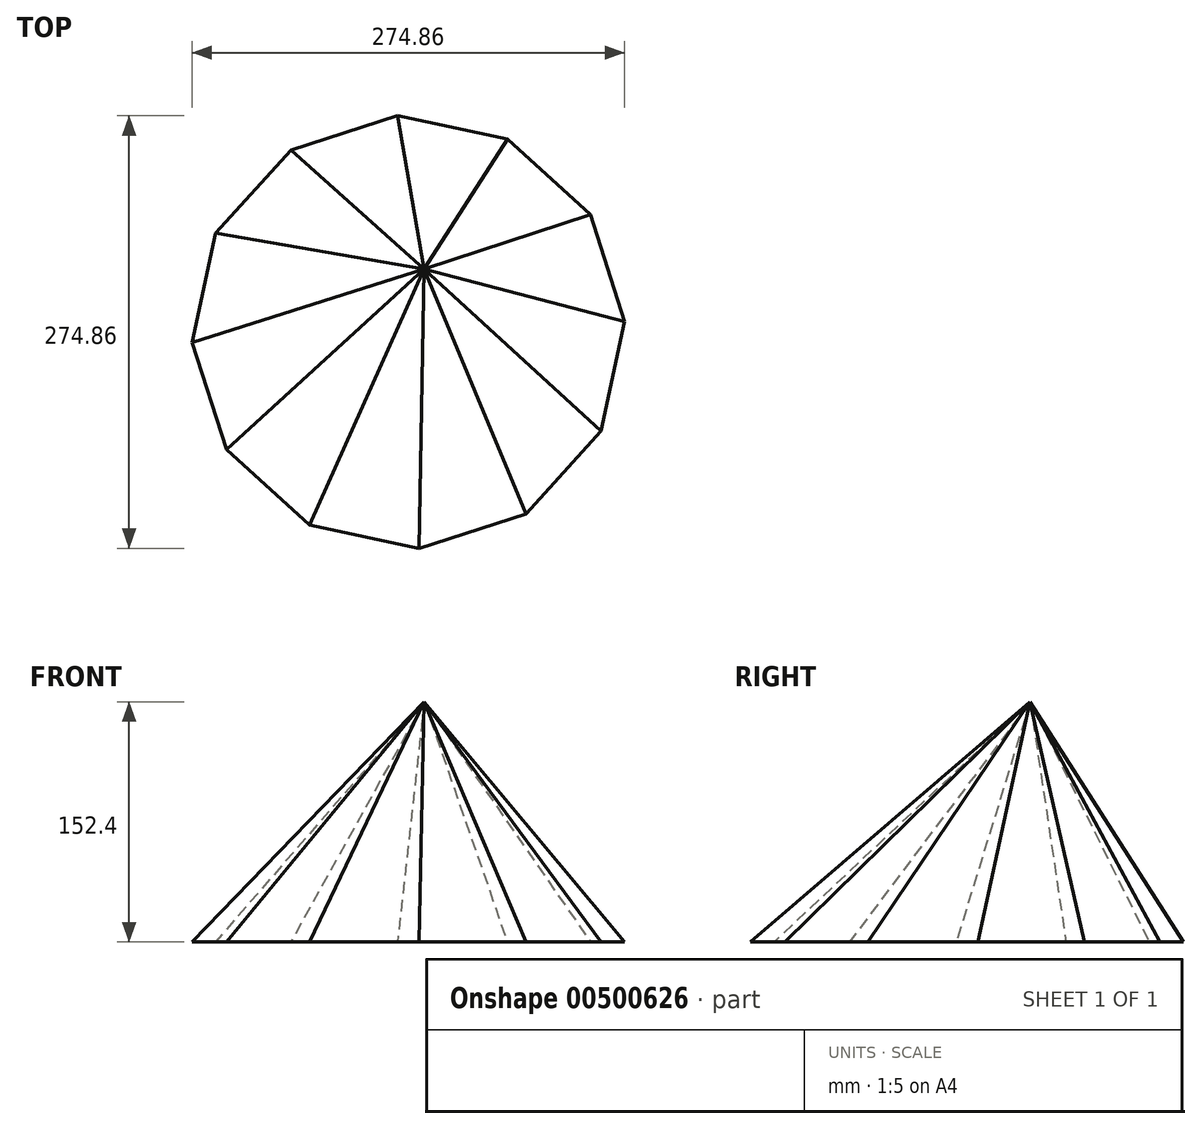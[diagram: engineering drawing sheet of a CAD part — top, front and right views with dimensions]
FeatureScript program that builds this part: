
annotation { "Feature Type Name" : "Feature", "Feature Type Description" : "" }
export const myFeature = defineFeature(function(context is Context, id is Id, definition is map)
    precondition{}
    {
        {
            var Q0;
            Q0=qCreatedBy(makeId("Top.planeOp"),FACE);
            var sketch = newSketch(context, id + "F0", { "sketchPlane" : qUnion([Q0])});
            skCircle(sketch, "E0.cCircle", {"center": v(0, 0) * mm, "radius": 137.6 * mm, "construction": true});
            skLineSegment(sketch, "E0.0", {"start": v(115.61, 74.6) * mm, "end": v(137.43, 6.8) * mm});
            skLineSegment(sketch, "E0.1", {"start": v(137.43, 6.8) * mm, "end": v(122.42, -62.82) * mm});
            skLineSegment(sketch, "E0.2", {"start": v(122.42, -62.82) * mm, "end": v(74.6, -115.61) * mm});
            skLineSegment(sketch, "E0.3", {"start": v(74.6, -115.61) * mm, "end": v(6.8, -137.43) * mm});
            skLineSegment(sketch, "E0.4", {"start": v(6.8, -137.43) * mm, "end": v(-62.82, -122.42) * mm});
            skLineSegment(sketch, "E0.5", {"start": v(-62.82, -122.42) * mm, "end": v(-115.61, -74.6) * mm});
            skLineSegment(sketch, "E0.6", {"start": v(-115.61, -74.6) * mm, "end": v(-137.43, -6.8) * mm});
            skLineSegment(sketch, "E0.7", {"start": v(-137.43, -6.8) * mm, "end": v(-122.42, 62.82) * mm});
            skLineSegment(sketch, "E0.8", {"start": v(-122.42, 62.82) * mm, "end": v(-74.6, 115.61) * mm});
            skLineSegment(sketch, "E0.9", {"start": v(-74.6, 115.61) * mm, "end": v(-6.8, 137.43) * mm});
            skLineSegment(sketch, "E0.10", {"start": v(-6.8, 137.43) * mm, "end": v(62.82, 122.42) * mm});
            skLineSegment(sketch, "E0.11", {"start": v(62.82, 122.42) * mm, "end": v(115.61, 74.6) * mm});
            skSolve(sketch);
        }
        {
            var Q0;
            Q0=qCreatedBy(makeId("Top.planeOp"),FACE);
            cPlane(context, id + "F1", {"entities" : qUnion([Q0]), "cplaneType" : CPlaneType.OFFSET, "offset" : 152.4 * mm, "width" : 152.4 * mm, "height" : 152.4 * mm});
        }
        {
            var Q0;
            Q0=qCreatedBy(id+"F1.planeOp",FACE);
            var sketch = newSketch(context, id + "F2", { "sketchPlane" : qUnion([Q0])});
            skPoint(sketch, "E1", {"position": v(10.07, 40.03) * mm});
            skSolve(sketch);
        }
        {
            var Q0;
            Q0=sQuery(id+"F2.wireOp",VERTEX,"E1");
            var Q1;
            Q1=makeQuery(id+"F0.imprint","IMPRINT",FACE,{"disambiguationData":[TD([[makeQuery(id+"F0.imprint","IMPRINT",EDGE,{"derivedFrom":sQuery(id+"F0.wireOp",EDGE,"E0.0")}),-1.0]])]});
            loft(context, id + "F3", {"sheetProfilesArray" : [{ "sheetProfileEntities" : qUnion([Q0]) }, { "sheetProfileEntities" : qUnion([Q1]) }]});
        }
    });
